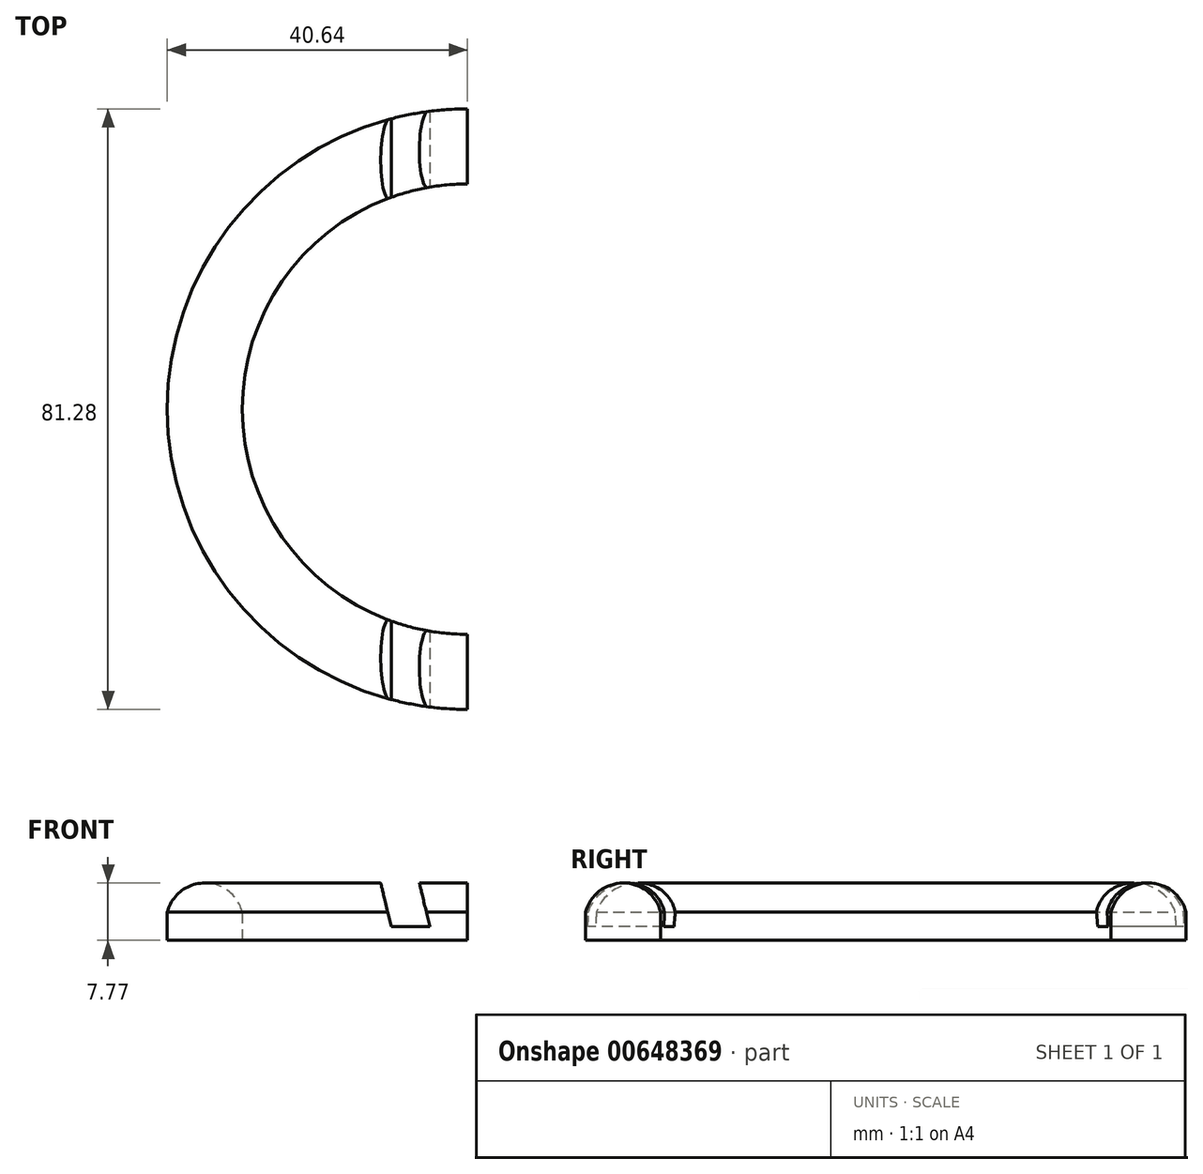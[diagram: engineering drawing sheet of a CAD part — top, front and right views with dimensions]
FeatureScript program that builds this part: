
annotation { "Feature Type Name" : "Feature", "Feature Type Description" : "" }
export const myFeature = defineFeature(function(context is Context, id is Id, definition is map)
    precondition{}
    {
        {
            var Q0;
            Q0=qCreatedBy(makeId("Front.planeOp"),FACE);
            var sketch = newSketch(context, id + "F0", { "sketchPlane" : qUnion([Q0])});
            skArc(sketch, "E0", {"start": v(-30.48, 0) * mm, "mid": v(-35.56, 3.96) * mm, "end": v(-40.64, 0) * mm});
            skLineSegment(sketch, "E1", {"start": v(0, 0) * mm, "end": v(0, 63.33) * mm, "construction": true});
            skLineSegment(sketch, "E2", {"start": v(-40.64, 0) * mm, "end": v(-40.64, -3.81) * mm});
            skLineSegment(sketch, "E3", {"start": v(-40.64, -3.81) * mm, "end": v(-30.48, -3.8) * mm});
            skLineSegment(sketch, "E4", {"start": v(-30.48, -3.8) * mm, "end": v(-30.48, 0) * mm});
            skSolve(sketch);
        }
        {
            var Q0;
            Q0 = qSketchRegion(id + "F0", true);
            var Q1;
            Q1=sQuery(id+"F0.wireOp",EDGE,"E1");
            revolve(context, id + "F1", {"entities" : qUnion([Q0]), "axis" : qUnion([Q1]), "revolveType" : RevolveType.SYMMETRIC, "angle" : 180 * degree});
        }
        {
            var Q0;
            Q0=qCreatedBy(makeId("Front.planeOp"),FACE);
            var sketch = newSketch(context, id + "F2", { "sketchPlane" : qUnion([Q0])});
            skLineSegment(sketch, "E5", {"start": v(-8.95, 14.03) * mm, "end": v(-5.08, -1.96) * mm});
            skLineSegment(sketch, "E6", {"start": v(-5.08, -1.96) * mm, "end": v(-10.3, -1.96) * mm});
            skLineSegment(sketch, "E7", {"start": v(-10.3, -1.96) * mm, "end": v(-13.82, 12.53) * mm});
            skLineSegment(sketch, "E8", {"start": v(-13.82, 12.53) * mm, "end": v(-8.95, 14.03) * mm});
            skSolve(sketch);
        }
        {
            var Q0;
            Q0 = qSketchRegion(id + "F2", true);
            extrude(context, id + "F3", {"entities" : qUnion([Q0]), "operationType" : NewBodyOperationType.REMOVE, "endBound" : BoundingType.SYMMETRIC, "oppositeDirection" : true, "depth" : 152.4 * mm, "offsetDistance" : 25.4 * mm});
        }
    });
